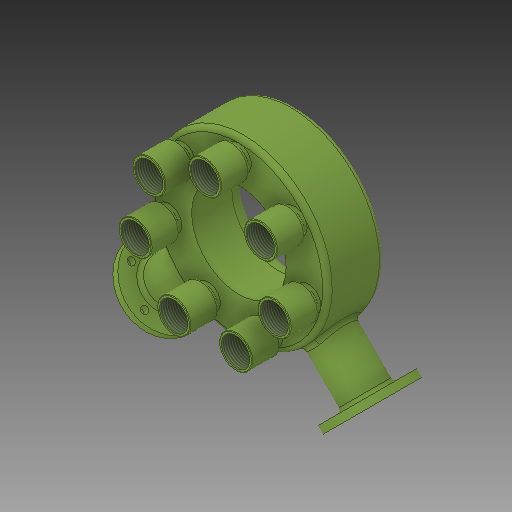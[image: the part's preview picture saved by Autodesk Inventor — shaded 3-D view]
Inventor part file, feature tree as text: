
AUTODESK INVENTOR PART (.ipt)
format: ipt  version: 2018 (Build 220112000, 112)  size: 720,896 bytes
history: native  units: mm
features: sketch x9, extrude x5, fillet x4, revolve x2, plane x2, pattern_circular x2, mirror x1, thread x1, other x1, projected_geometry x1
ambient origin geometry x8: Origin, YZ Plane, XZ Plane, XY Plane, X Axis, Y Axis, Z Axis, Center Point
bodies: Solid1 (feature_tree)
feature tree (28):
  revolve  "Revolution1"  [1 undecoded]
  plane  "Work Plane1"
  sketch  "Sketch2"  dims[d2=20.0mm d3=1.5mm]
  sketch  "Sketch3"  dims[d4=1.5mm d5=2.0mm]
  plane  "Work Plane2"
  extrude  "Extrusion1"  Depth=1.5mm
  extrude  "Extrusion2"  Depth=1.5mm
  extrude  "Extrusion3"  Depth=5.0mm
  fillet  "Fillet1"  Radius=2.0mm
  fillet  "Fillet2"  Radius=5.0mm
  fillet  "Fillet3"  Radius=7.0mm
  extrude  "Extrusion4"  [1 undecoded]
  pattern_circular  "Circular Pattern1"  Count=6  [1 undecoded]
  mirror  "Mirror1"
  revolve  "Revolution2"  Angle=45.0deg
  extrude  "Extrusion5"  Depth=18.0mm
  fillet  "Fillet4"  Radius=10.0mm
  thread  "Thread1"  [1 undecoded]
  other  "Work Axis1"
  pattern_circular  "Circular Pattern2"  [2 undecoded]
  sketch  "Sketch1"  dims[d0=24.0mm d1=37.5mm]
  sketch  "Sketch4"  dims[d6=2.0mm d7=1.0mm d8=2.0mm d9=5.0mm d10=7.0mm]
  sketch  "Sketch5"  dims[d11=90.0deg d12=-12.0mm d13=60.0mm]
  sketch  "Sketch6"  dims[d14=45.0deg d15=45.0deg]
  sketch  "Sketch7"  dims[d16=15.0mm d17=18.0mm d18=10.0mm d19=0.0mm d20=34.0mm]
  sketch  "Sketch8"  dims[d21=3.0mm d22=0.0mm]
  sketch  "Sketch9"  dims[d23=32.75mm d24=0.0mm d25=4.0mm d26=1.5mm d27=2.0mm d28=13.0mm d29=3.0mm d30=6.75mm d31=0.0mm d32=50.0mm d33=360.0deg d36=2.0mm d37=30.2mm d38=3.5mm d39=4.5mm d40=6.0mm d41=7.0mm d43=12.5mm d44=11.5mm d45=0.25mm d46=0.25mm d47=1.25mm d48=1.0mm d49=90.0deg d50=10.25mm d51=0.0mm d52=1.5mm d53=10.0mm d54=0.0mm d55=70.0mm d56=360.0deg]
  projected_geometry  "Projected Loop1"
note: 6 required parameter values undecoded (feature->parameter linkage not recoverable at this tier; creation-order binding heuristic only, values carry confidence <= 0.55)